# Revit family: Zumtobel SLOTLIGHT INF slim
name_source: partatom
category: Lighting Fixtures
revit_build: Autodesk Revit 2016 (Build: 20150220_1215(x64)
units: mm (PartAtom-declared; Revit-internal decimal feet)

## family parameters
Cut with Voids When Loaded = No
Host = Face
Light Source = Yes
OmniClass Number = 23.80.70.11
OmniClass Title = Luminaries for Internal Lighting
Part Type = Normal
Room Calculation Point = No
Round Connector Dimension = Use Diameter
Shared = No

## types (13) — shared parameters
Assembly Code = D5020200
Body = Zumtobel_Metal_White
Color Filter = 16777215
Color Light Emitting Surface = Zumtobel_PMMA_White
Description = SLOTLIGHT infinity slim single luminaire
Dimming Lamp Color Temperature Shift = <None>
Emit Shape Visible in Rendering = No
Emit from Rectangle Length = 45 mm  [stored 0.147638 ft]
Height = 64 mm  [stored 0.209974 ft]
Lamp = LED
Manufacturer = Zumtobel Lighting
Tilt Angle = -90.00°
URL = http://www.zumtobel.com
Width = 45 mm  [stored 0.147638 ft]
zero-valued in all types: Default Elevation

## per-type parameters (varying)
| type | Apparent Load | Emit from Rectangle Width | Length | Model | Photometric Web File |
| SLOIN slim SL LED1800 L1004 | 25 VA | 1004 mm  [stored 3.29396 ft] | 1004 mm  [stored 3.29396 ft] | 42183860 | D36769AA_SLOIN_SLIM_CL_LED2400-840_L775_PC.IES |
| SLOIN slim SL LED2200 L1254 | 30 VA | 1254 mm  [stored 4.11417 ft] | 1254 mm  [stored 4.11417 ft] | 42183861 | D36769AA_SLOIN_slim_SL_LED2200-840_L1254_PC.IES |
| SLOIN slim SL LED2600 L1504 | 36 VA | 1504 mm  [stored 4.93438 ft] | 1504 mm  [stored 4.93438 ft] | 42183879 | D36769AA_SLOIN_slim_SL_LED2600-840_L1504_PC.IES |
| SLOIN slim SL LED3000 L1754 | 42 VA | 1754 mm  [stored 5.75459 ft] | 1754 mm  [stored 5.75459 ft] | 42183884 | D36769AA_SLOIN_slim_SL_LED3000-840_L1754_PC.IES |
| SLOIN slim SL LED3400 L2004 | 48 VA | 2004 mm  [stored 6.5748 ft] | 2004 mm  [stored 6.5748 ft] | 42183885 | D36769AA_SLOIN_slim_SL_LED3400-840_L2004_PC.IES |
| SLOIN slim SL LED3800 L2254 | 52 VA | 2254 mm  [stored 7.39501 ft] | 2254 mm  [stored 7.39501 ft] | 42183886 | D36769AA_SLOIN_slim_SL_LED3800-840_L2254_PC.IES |
| SLOIN slim SL LED4200 L2504 | 57 VA | 2504 mm  [stored 8.21522 ft] | 2504 mm  [stored 8.21522 ft] | 42183887 | D36769AA_SLOIN_slim_SL_LED4200-840_L2504_PC.IES |
| SLOIN slim SL LED4600 L2754 | 63 VA | 2754 mm  [stored 9.03543 ft] | 2754 mm  [stored 9.03543 ft] | 42183888 | D36769AA_SLOIN_slim_SL_LED4600-840_L2754_PC.IES |
| SLOIN slim SL LED5000 L3004 | 69 VA | 3004 mm  [stored 9.85564 ft] | 3004 mm  [stored 9.85564 ft] | 42183889 | D36769AA_SLOIN_slim_SL_LED5000-840_L3004_PC.IES |
| SLOIN slim SL LED5400 L3254 | 74 VA | 3254 mm  [stored 10.6759 ft] | 3254 mm  [stored 10.6759 ft] | 42183890 | D36769AA_SLOIN_slim_SL_LED5400-840_L3254_PC.IES |
| SLOIN slim SL LED5800 L3504 | 80 VA | 3504 mm  [stored 11.4961 ft] | 3504 mm  [stored 11.4961 ft] | 42183891 | D36769AA_SLOIN_slim_SL_LED5800-840_L3504_PC.IES |
| SLOIN slim SL LED6200 L3754 | 86 VA | 3754 mm  [stored 12.3163 ft] | 3754 mm  [stored 12.3163 ft] | 42183892 | D36769AA_SLOIN_slim_SL_LED6200-840_L3754_PC.IES |
| SLOIN slim SL LED6600 L4004 | 91 VA | 4004 mm  [stored 13.1365 ft] | 4004 mm  [stored 13.1365 ft] | 42183893 | D36769AA_SLOIN_slim_SL_LED6600-840_L4004_PC.IES |

note: [stored X ft] marks values corroborated as IEEE doubles in the binary element streams (Revit-internal decimal feet)

## geometry (parser evidence)
native form markers: Blend x4, Sweep x10
no freeform markers — native parametric forms only
